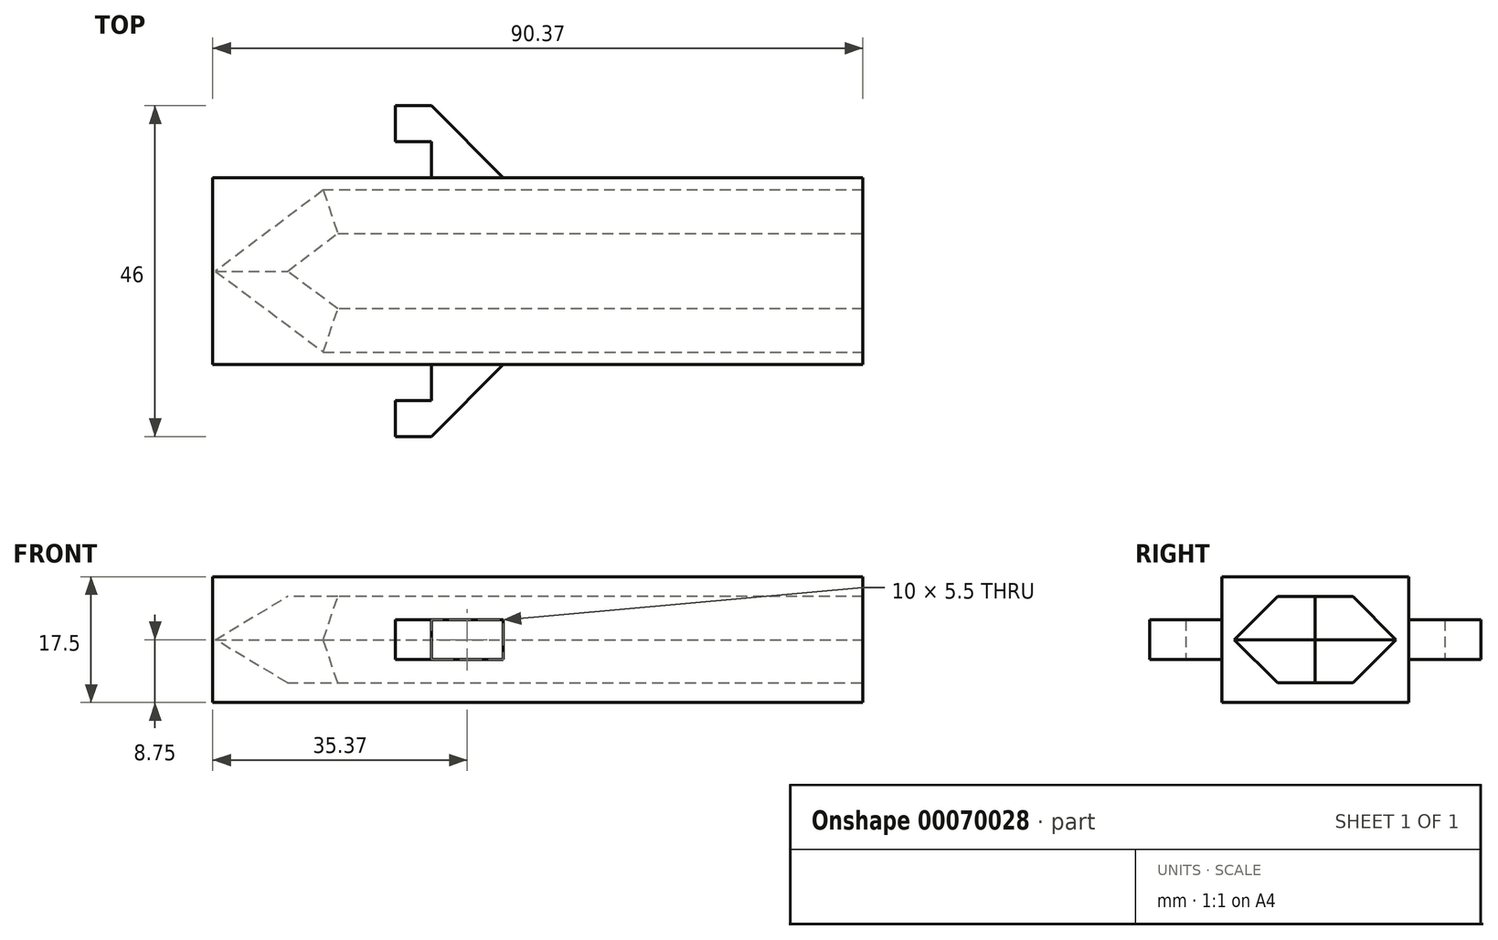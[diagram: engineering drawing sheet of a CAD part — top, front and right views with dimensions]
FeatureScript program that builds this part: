
annotation { "Feature Type Name" : "Feature", "Feature Type Description" : "" }
export const myFeature = defineFeature(function(context is Context, id is Id, definition is map)
    precondition{}
    {
        {
            var Q0;
            Q0=qCreatedBy(makeId("Top.planeOp"),FACE);
            var sketch = newSketch(context, id + "F0", { "sketchPlane" : qUnion([Q0])});
            skLineSegment(sketch, "E0.bottom", {"start": v(0, 0) * mm, "end": v(91, 0) * mm});
            skLineSegment(sketch, "E0.top", {"start": v(0, 21) * mm, "end": v(91, 21) * mm});
            skLineSegment(sketch, "E0.left", {"start": v(0, 0) * mm, "end": v(0, 21) * mm});
            skLineSegment(sketch, "E0.right", {"start": v(91, 0) * mm, "end": v(91, 21) * mm});
            skLineSegment(sketch, "E1", {"start": v(0, 10.5) * mm, "end": v(15, 10.5) * mm});
            skLineSegment(sketch, "E2", {"start": v(0, 10.5) * mm, "end": v(15, 21) * mm});
            skLineSegment(sketch, "E3", {"start": v(0, 10.5) * mm, "end": v(15, 0) * mm});
            skSolve(sketch);
        }
        {
            var Q0;
            Q0 = qSketchRegion(id + "F0", true);
            extrude(context, id + "F1", {"entities" : qUnion([Q0]), "depth" : 10 * mm});
        }
        {
            var Q0;
            Q0=makeQuery(id+"F1.opExtrude","SWEPT_FACE",FACE,{"disambiguationData":[OSD([sQuery(id+"F0.wireOp",EDGE,"E0.left")])]});
            var sketch = newSketch(context, id + "F2", { "sketchPlane" : qUnion([Q0])});
            skSolve(sketch);
        }
        {
            var Q0;
            Q0 = qSketchRegion(id + "F2", true);
            var Q1;
            {var subQ0=sQuery(id+"F0.wireOp",EDGE,"E0.left");Q1=makeQuery(id+"F2.imprint","IMPRINT",FACE,{"disambiguationData":[TD([[makeQuery(id+"F2.imprint","IMPRINT",EDGE,{"derivedFrom":makeQuery(id+"F1.opExtrude","CAP_EDGE",EDGE,{"disambiguationData":[OSD([subQ0])],"isStart":true})}),-1.0]])]});}
            extrude(context, id + "F3", {"entities" : qUnion([Q0, Q1]), "operationType" : NewBodyOperationType.ADD, "depth" : 9 * mm});
        }
        {
            var Q0;
            {var subQ0=sQuery(id+"F0.wireOp",EDGE,"E0.left");Q0=makeQuery(id+"F3.boolean.opBoolean","MERGE",FACE,{"derivedFrom":[makeQuery(id+"F1.opExtrude","CAP_FACE",FACE,{"disambiguationData":[OSD([sQuery(id+"F0.wireOp",EDGE,"E0.bottom"),sQuery(id+"F0.wireOp",EDGE,"E0.top"),subQ0,sQuery(id+"F0.wireOp",EDGE,"E0.right")])],"isStart":false}),makeQuery(id+"F3.opExtrude","SWEPT_FACE",FACE,{"disambiguationData":[OSD([subQ0]),TDD([makeQuery(id+"F2.imprint","IMPRINT",EDGE,{"derivedFrom":makeQuery(id+"F1.opExtrude","CAP_EDGE",EDGE,{"disambiguationData":[OSD([subQ0])],"isStart":false})})])]})]});}
            extrude(context, id + "F4", {"entities" : qUnion([Q0]), "operationType" : NewBodyOperationType.ADD, "depth" : 2 * mm});
        }
        {
            var Q0;
            Q0=makeQuery(id+"F4.opExtrude","CAP_FACE",FACE,{"disambiguationData":[OSD([sQuery(id+"F0.wireOp",EDGE,"E0.bottom"),sQuery(id+"F0.wireOp",EDGE,"E0.top"),sQuery(id+"F0.wireOp",EDGE,"E0.left"),sQuery(id+"F0.wireOp",EDGE,"E0.right")])],"isStart":false});
            extrude(context, id + "F5", {"entities" : qUnion([Q0]), "operationType" : NewBodyOperationType.ADD, "depth" : 3 * mm});
        }
        {
            var Q0;
            {var subQ0=sQuery(id+"F0.wireOp",EDGE,"E0.left");var subQ1=sQuery(id+"F0.wireOp",EDGE,"E0.top");Q0=makeQuery(id+"F5.boolean.opBoolean","MERGE",FACE,{"derivedFrom":[makeQuery(id+"F4.boolean.opBoolean","MERGE",FACE,{"derivedFrom":[makeQuery(id+"F3.boolean.opBoolean","MERGE",FACE,{"derivedFrom":[makeQuery(id+"F1.opExtrude","SWEPT_FACE",FACE,{"disambiguationData":[OSD([subQ1])]}),makeQuery(id+"F3.opExtrude","SWEPT_FACE",FACE,{"disambiguationData":[OSD([subQ1,subQ0])]})]}),makeQuery(id+"F4.opExtrude","SWEPT_FACE",FACE,{"disambiguationData":[OSD([subQ1,subQ0])]})]}),makeQuery(id+"F5.opExtrude","SWEPT_FACE",FACE,{"disambiguationData":[OSD([subQ1,subQ0])]})]});}
            extrude(context, id + "F6", {"entities" : qUnion([Q0]), "operationType" : NewBodyOperationType.ADD, "depth" : 5 * mm});
        }
        {
            var Q0;
            {var subQ0=sQuery(id+"F0.wireOp",EDGE,"E0.left");var subQ1=sQuery(id+"F0.wireOp",EDGE,"E0.top");Q0=makeQuery(id+"F6.boolean.opBoolean","MERGE",FACE,{"derivedFrom":[makeQuery(id+"F5.opExtrude","CAP_FACE",FACE,{"disambiguationData":[OSD([sQuery(id+"F0.wireOp",EDGE,"E0.bottom"),subQ1,subQ0,sQuery(id+"F0.wireOp",EDGE,"E0.right")])],"isStart":false}),makeQuery(id+"F6.opExtrude","SWEPT_FACE",FACE,{"disambiguationData":[OSD([subQ1,subQ0]),TDD([makeQuery(id+"F5.opExtrude","CAP_EDGE",EDGE,{"disambiguationData":[OSD([subQ1,subQ0])],"isStart":false})])]})]});}
            extrude(context, id + "F7", {"entities" : qUnion([Q0]), "operationType" : NewBodyOperationType.ADD, "depth" : 2.5 * mm});
        }
        {
            var Q0;
            {var subQ0=sQuery(id+"F0.wireOp",EDGE,"E0.right");var subQ1=sQuery(id+"F0.wireOp",EDGE,"E0.top");Q0=makeQuery(id+"F7.boolean.opBoolean","MERGE",FACE,{"derivedFrom":[makeQuery(id+"F6.boolean.opBoolean","MERGE",FACE,{"derivedFrom":[makeQuery(id+"F5.boolean.opBoolean","MERGE",FACE,{"derivedFrom":[makeQuery(id+"F4.boolean.opBoolean","MERGE",FACE,{"derivedFrom":[makeQuery(id+"F1.opExtrude","SWEPT_FACE",FACE,{"disambiguationData":[OSD([subQ0])]}),makeQuery(id+"F4.opExtrude","SWEPT_FACE",FACE,{"disambiguationData":[OSD([subQ0])]})]}),makeQuery(id+"F5.opExtrude","SWEPT_FACE",FACE,{"disambiguationData":[OSD([subQ0])]})]}),makeQuery(id+"F6.opExtrude","SWEPT_FACE",FACE,{"disambiguationData":[OSD([subQ1,subQ0])]})]}),makeQuery(id+"F7.opExtrude","SWEPT_FACE",FACE,{"disambiguationData":[OSD([subQ1,subQ0])]})]});}
            var sketch = newSketch(context, id + "F8", { "sketchPlane" : qUnion([Q0])});
            skLineSegment(sketch, "E4.bottom", {"start": v(1.75, 14.75) * mm, "end": v(24.25, 14.75) * mm});
            skLineSegment(sketch, "E4.top", {"start": v(1.75, 2.75) * mm, "end": v(24.25, 2.75) * mm});
            skLineSegment(sketch, "E4.left", {"start": v(1.75, 14.75) * mm, "end": v(1.75, 2.75) * mm});
            skLineSegment(sketch, "E4.right", {"start": v(24.25, 14.75) * mm, "end": v(24.25, 2.75) * mm});
            skSolve(sketch);
        }
        {
            var Q0;
            Q0 = qSketchRegion(id + "F8", true);
            extrude(context, id + "F9", {"entities" : qUnion([Q0]), "operationType" : NewBodyOperationType.REMOVE, "oppositeDirection" : true, "depth" : 75 * mm});
        }
        {
            var Q0;
            Q0=makeQuery(id+"F9.boolean.opBoolean","COPY",FACE,{"derivedFrom":makeQuery(id+"F9.opExtrude","SWEPT_FACE",FACE,{"disambiguationData":[OSD([sQuery(id+"F8.wireOp",EDGE,"E4.top")])]})});
            var sketch = newSketch(context, id + "F10", { "sketchPlane" : qUnion([Q0])});
            skLineSegment(sketch, "E5", {"start": v(16, 13) * mm, "end": v(1, 13) * mm});
            skLineSegment(sketch, "E6", {"start": v(1, 13) * mm, "end": v(16, 24.25) * mm});
            skLineSegment(sketch, "E7", {"start": v(16, 24.25) * mm, "end": v(16, 1.75) * mm});
            skLineSegment(sketch, "E8", {"start": v(16, 1.75) * mm, "end": v(1, 13) * mm});
            skSolve(sketch);
        }
        {
            var Q0;
            Q0 = qSketchRegion(id + "F10", true);
            extrude(context, id + "F11", {"entities" : qUnion([Q0]), "operationType" : NewBodyOperationType.REMOVE, "depth" : 12 * mm});
        }
        {
            var Q0;
            Q0=makeQuery(id+"F11.boolean.opBoolean","COPY",EDGE,{"derivedFrom":makeQuery(id+"F11.opExtrude","CAP_EDGE",EDGE,{"disambiguationData":[OSD([sQuery(id+"F10.wireOp",EDGE,"E8")])],"isStart":false})});
            var Q1;
            Q1=makeQuery(id+"F11.boolean.opBoolean","COPY",EDGE,{"derivedFrom":makeQuery(id+"F11.opExtrude","CAP_EDGE",EDGE,{"disambiguationData":[OSD([sQuery(id+"F10.wireOp",EDGE,"E6")])],"isStart":false})});
            var Q2;
            Q2=makeQuery(id+"F11.boolean.opBoolean","COPY",EDGE,{"derivedFrom":makeQuery(id+"F11.opExtrude","CAP_EDGE",EDGE,{"disambiguationData":[OSD([sQuery(id+"F10.wireOp",EDGE,"E8")])],"isStart":true})});
            var Q3;
            Q3=makeQuery(id+"F11.boolean.opBoolean","COPY",EDGE,{"derivedFrom":makeQuery(id+"F11.opExtrude","CAP_EDGE",EDGE,{"disambiguationData":[OSD([sQuery(id+"F10.wireOp",EDGE,"E6")])],"isStart":true})});
            var Q4;
            Q4=makeQuery(id+"F9.boolean.opBoolean","COPY",EDGE,{"derivedFrom":makeQuery(id+"F9.opExtrude","SWEPT_EDGE",EDGE,{"disambiguationData":[OSD([sQuery(id+"F8.wireOp",EDGE,"E4.top"),sQuery(id+"F8.wireOp",EDGE,"E4.left")])]})});
            var Q5;
            Q5=makeQuery(id+"F9.boolean.opBoolean","COPY",EDGE,{"derivedFrom":makeQuery(id+"F9.opExtrude","SWEPT_EDGE",EDGE,{"disambiguationData":[OSD([sQuery(id+"F8.wireOp",EDGE,"E4.bottom"),sQuery(id+"F8.wireOp",EDGE,"E4.left")])]})});
            var Q6;
            Q6=makeQuery(id+"F9.boolean.opBoolean","COPY",EDGE,{"derivedFrom":makeQuery(id+"F9.opExtrude","SWEPT_EDGE",EDGE,{"disambiguationData":[OSD([sQuery(id+"F8.wireOp",EDGE,"E4.bottom"),sQuery(id+"F8.wireOp",EDGE,"E4.right")])]})});
            var Q7;
            Q7=makeQuery(id+"F9.boolean.opBoolean","COPY",EDGE,{"derivedFrom":makeQuery(id+"F9.opExtrude","SWEPT_EDGE",EDGE,{"disambiguationData":[OSD([sQuery(id+"F8.wireOp",EDGE,"E4.top"),sQuery(id+"F8.wireOp",EDGE,"E4.right")])]})});
            chamfer(context, id + "F12", {"entities" : qUnion([Q0, Q1, Q2, Q3, Q4, Q5, Q6, Q7]), "width" : 6 * mm, "tangentPropagation" : true});
        }
        {
            var Q0;
            {var subQ0=sQuery(id+"F0.wireOp",EDGE,"E0.left");var subQ1=sQuery(id+"F0.wireOp",EDGE,"E0.top");Q0=makeQuery(id+"F7.boolean.opBoolean","MERGE",FACE,{"derivedFrom":[makeQuery(id+"F6.opExtrude","CAP_FACE",FACE,{"disambiguationData":[OSD([subQ1,subQ0])],"isStart":false}),makeQuery(id+"F7.opExtrude","SWEPT_FACE",FACE,{"disambiguationData":[OSD([subQ1,subQ0]),TDD([makeQuery(id+"F6.opExtrude","CAP_EDGE",EDGE,{"disambiguationData":[OSD([subQ1,subQ0]),TDD([makeQuery(id+"F5.opExtrude","CAP_EDGE",EDGE,{"disambiguationData":[OSD([subQ1,subQ0])],"isStart":false})])],"isStart":false})])]})]});}
            var sketch = newSketch(context, id + "F13", { "sketchPlane" : qUnion([Q0])});
            skPoint(sketch, "E9.firstSnap0", {"position": v(-41, 17.5) * mm});
            skLineSegment(sketch, "E9.bottom", {"start": v(-41, 11.5) * mm, "end": v(-26, 11.5) * mm});
            skLineSegment(sketch, "E9.top", {"start": v(-41, 6) * mm, "end": v(-26, 6) * mm});
            skLineSegment(sketch, "E9.left", {"start": v(-41, 11.5) * mm, "end": v(-41, 6) * mm});
            skLineSegment(sketch, "E9.right", {"start": v(-26, 11.5) * mm, "end": v(-26, 6) * mm});
            skLineSegment(sketch, "E10", {"start": v(-91, 17.5) * mm, "end": v(-91, 0) * mm});
            skSolve(sketch);
        }
        {
            var Q0;
            Q0 = qSketchRegion(id + "F13", true);
            extrude(context, id + "F14", {"entities" : qUnion([Q0]), "operationType" : NewBodyOperationType.ADD, "depth" : 10 * mm});
        }
        {
            var Q0;
            Q0=makeQuery(id+"F14.opExtrude","CAP_EDGE",EDGE,{"disambiguationData":[OSD([sQuery(id+"F13.wireOp",EDGE,"E9.left")])],"isStart":false});
            chamfer(context, id + "F15", {"entities" : qUnion([Q0]), "width" : 10 * mm, "tangentPropagation" : true});
        }
        {
            var Q0;
            Q0=makeQuery(id+"F14.opExtrude","SWEPT_FACE",FACE,{"disambiguationData":[OSD([sQuery(id+"F13.wireOp",EDGE,"E9.right")])]});
            var sketch = newSketch(context, id + "F16", { "sketchPlane" : qUnion([Q0])});
            skLineSegment(sketch, "E11.bottom", {"start": v(-31, 11.5) * mm, "end": v(-26, 11.5) * mm});
            skLineSegment(sketch, "E11.top", {"start": v(-31, 6) * mm, "end": v(-26, 6) * mm});
            skLineSegment(sketch, "E11.left", {"start": v(-31, 11.5) * mm, "end": v(-31, 6) * mm});
            skLineSegment(sketch, "E11.right", {"start": v(-26, 11.5) * mm, "end": v(-26, 6) * mm});
            skSolve(sketch);
        }
        {
            var Q0;
            Q0 = qSketchRegion(id + "F16", true);
            extrude(context, id + "F17", {"entities" : qUnion([Q0]), "operationType" : NewBodyOperationType.REMOVE, "oppositeDirection" : true, "depth" : 5 * mm});
        }
        {
            var Q0;
            {var subQ0=sQuery(id+"F0.wireOp",EDGE,"E0.left");var subQ1=sQuery(id+"F0.wireOp",EDGE,"E0.bottom");Q0=makeQuery(id+"F7.boolean.opBoolean","MERGE",FACE,{"derivedFrom":[makeQuery(id+"F5.boolean.opBoolean","MERGE",FACE,{"derivedFrom":[makeQuery(id+"F4.boolean.opBoolean","MERGE",FACE,{"derivedFrom":[makeQuery(id+"F3.boolean.opBoolean","MERGE",FACE,{"derivedFrom":[makeQuery(id+"F1.opExtrude","SWEPT_FACE",FACE,{"disambiguationData":[OSD([subQ1])]}),makeQuery(id+"F3.opExtrude","SWEPT_FACE",FACE,{"disambiguationData":[OSD([subQ1,subQ0])]})]}),makeQuery(id+"F4.opExtrude","SWEPT_FACE",FACE,{"disambiguationData":[OSD([subQ1,subQ0])]})]}),makeQuery(id+"F5.opExtrude","SWEPT_FACE",FACE,{"disambiguationData":[OSD([subQ1,subQ0])]})]}),makeQuery(id+"F7.opExtrude","SWEPT_FACE",FACE,{"disambiguationData":[OSD([subQ1,subQ0])]})]});}
            var sketch = newSketch(context, id + "F18", { "sketchPlane" : qUnion([Q0])});
            skPoint(sketch, "E12.firstSnap0", {"position": v(41, 17.5) * mm});
            skLineSegment(sketch, "E12.bottom", {"start": v(41, 11.5) * mm, "end": v(26, 11.5) * mm});
            skLineSegment(sketch, "E12.top", {"start": v(41, 6) * mm, "end": v(26, 6) * mm});
            skLineSegment(sketch, "E12.left", {"start": v(41, 11.5) * mm, "end": v(41, 6) * mm});
            skLineSegment(sketch, "E12.right", {"start": v(26, 11.5) * mm, "end": v(26, 6) * mm});
            skSolve(sketch);
        }
        {
            var Q0;
            Q0 = qSketchRegion(id + "F18", true);
            extrude(context, id + "F19", {"entities" : qUnion([Q0]), "operationType" : NewBodyOperationType.ADD, "depth" : 10 * mm});
        }
        {
            var Q0;
            Q0=makeQuery(id+"F19.opExtrude","CAP_EDGE",EDGE,{"disambiguationData":[OSD([sQuery(id+"F18.wireOp",EDGE,"E12.left")])],"isStart":false});
            chamfer(context, id + "F20", {"entities" : qUnion([Q0]), "width" : 10 * mm, "tangentPropagation" : true});
        }
        {
            var Q0;
            Q0=makeQuery(id+"F19.opExtrude","SWEPT_FACE",FACE,{"disambiguationData":[OSD([sQuery(id+"F18.wireOp",EDGE,"E12.right")])]});
            var sketch = newSketch(context, id + "F21", { "sketchPlane" : qUnion([Q0])});
            skLineSegment(sketch, "E13.bottom", {"start": v(0, 11.5) * mm, "end": v(5, 11.5) * mm});
            skLineSegment(sketch, "E13.top", {"start": v(0, 6) * mm, "end": v(5, 6) * mm});
            skLineSegment(sketch, "E13.left", {"start": v(0, 11.5) * mm, "end": v(0, 6) * mm});
            skLineSegment(sketch, "E13.right", {"start": v(5, 11.5) * mm, "end": v(5, 6) * mm});
            skSolve(sketch);
        }
        {
            var Q0;
            Q0 = qSketchRegion(id + "F21", true);
            extrude(context, id + "F22", {"entities" : qUnion([Q0]), "operationType" : NewBodyOperationType.REMOVE, "oppositeDirection" : true, "depth" : 5 * mm});
        }
        {
            var Q0;
            {var subQ0=sQuery(id+"F0.wireOp",EDGE,"E0.left");var subQ1=sQuery(id+"F0.wireOp",EDGE,"E0.top");Q0=makeQuery(id+"F7.boolean.opBoolean","MERGE",FACE,{"derivedFrom":[makeQuery(id+"F6.boolean.opBoolean","MERGE",FACE,{"derivedFrom":[makeQuery(id+"F5.boolean.opBoolean","MERGE",FACE,{"derivedFrom":[makeQuery(id+"F4.boolean.opBoolean","MERGE",FACE,{"derivedFrom":[makeQuery(id+"F3.opExtrude","CAP_FACE",FACE,{"disambiguationData":[OSD([sQuery(id+"F0.wireOp",EDGE,"E0.bottom"),subQ1,subQ0])],"isStart":false}),makeQuery(id+"F4.opExtrude","SWEPT_FACE",FACE,{"disambiguationData":[OSD([subQ0])]})]}),makeQuery(id+"F5.opExtrude","SWEPT_FACE",FACE,{"disambiguationData":[OSD([subQ0])]})]}),makeQuery(id+"F6.opExtrude","SWEPT_FACE",FACE,{"disambiguationData":[OSD([subQ1,subQ0]),TDD([makeQuery(id+"F5.boolean.opBoolean","MERGE",EDGE,{"derivedFrom":[makeQuery(id+"F4.boolean.opBoolean","MERGE",EDGE,{"derivedFrom":[makeQuery(id+"F3.opExtrude","CAP_EDGE",EDGE,{"disambiguationData":[OSD([subQ1,subQ0])],"isStart":false}),makeQuery(id+"F4.opExtrude","SWEPT_EDGE",EDGE,{"disambiguationData":[OSD([subQ1,subQ0])]})]}),makeQuery(id+"F5.opExtrude","SWEPT_EDGE",EDGE,{"disambiguationData":[OSD([subQ1,subQ0])]})]})])]})]}),makeQuery(id+"F7.opExtrude","SWEPT_FACE",FACE,{"disambiguationData":[OSD([subQ1,subQ0]),TDD([makeQuery(id+"F6.boolean.opBoolean","MERGE",EDGE,{"derivedFrom":[makeQuery(id+"F5.opExtrude","CAP_EDGE",EDGE,{"disambiguationData":[OSD([subQ0])],"isStart":false}),makeQuery(id+"F6.opExtrude","SWEPT_EDGE",EDGE,{"disambiguationData":[OSD([subQ1,subQ0]),TDD([makeQuery(id+"F5.opExtrude","CAP_VERTEX",VERTEX,{"disambiguationData":[OSD([subQ1,subQ0])],"isStart":false})])]})]})])]})]});}
            extrude(context, id + "F23", {"entities" : qUnion([Q0]), "operationType" : NewBodyOperationType.ADD, "depth" : 5 * mm});
        }
        {
            var Q0;
            {var subQ0=sQuery(id+"F0.wireOp",EDGE,"E0.left");var subQ1=sQuery(id+"F0.wireOp",EDGE,"E0.top");Q0=makeQuery(id+"F23.opExtrude","CAP_EDGE",EDGE,{"disambiguationData":[OSD([subQ1,subQ0]),TDD([makeQuery(id+"F7.boolean.opBoolean","MERGE",EDGE,{"derivedFrom":[makeQuery(id+"F6.opExtrude","CAP_EDGE",EDGE,{"disambiguationData":[OSD([subQ1,subQ0]),TDD([makeQuery(id+"F5.boolean.opBoolean","MERGE",EDGE,{"derivedFrom":[makeQuery(id+"F4.boolean.opBoolean","MERGE",EDGE,{"derivedFrom":[makeQuery(id+"F3.opExtrude","CAP_EDGE",EDGE,{"disambiguationData":[OSD([subQ1,subQ0])],"isStart":false}),makeQuery(id+"F4.opExtrude","SWEPT_EDGE",EDGE,{"disambiguationData":[OSD([subQ1,subQ0])]})]}),makeQuery(id+"F5.opExtrude","SWEPT_EDGE",EDGE,{"disambiguationData":[OSD([subQ1,subQ0])]})]})])],"isStart":false}),makeQuery(id+"F7.opExtrude","SWEPT_EDGE",EDGE,{"disambiguationData":[OSD([subQ1,subQ0])]})]})])],"isStart":false});}
            var Q1;
            {var subQ0=sQuery(id+"F0.wireOp",EDGE,"E0.left");var subQ1=sQuery(id+"F0.wireOp",EDGE,"E0.top");Q1=makeQuery(id+"F23.opExtrude","CAP_EDGE",EDGE,{"disambiguationData":[OSD([subQ1,subQ0]),TDD([makeQuery(id+"F7.opExtrude","CAP_EDGE",EDGE,{"disambiguationData":[OSD([subQ1,subQ0]),TDD([makeQuery(id+"F6.boolean.opBoolean","MERGE",EDGE,{"derivedFrom":[makeQuery(id+"F5.opExtrude","CAP_EDGE",EDGE,{"disambiguationData":[OSD([subQ0])],"isStart":false}),makeQuery(id+"F6.opExtrude","SWEPT_EDGE",EDGE,{"disambiguationData":[OSD([subQ1,subQ0]),TDD([makeQuery(id+"F5.opExtrude","CAP_VERTEX",VERTEX,{"disambiguationData":[OSD([subQ1,subQ0])],"isStart":false})])]})]})])],"isStart":false})])],"isStart":false});}
            var Q2;
            Q2=makeQuery(id+"F23.opExtrude","CAP_EDGE",EDGE,{"disambiguationData":[OSD([sQuery(id+"F0.wireOp",EDGE,"E0.bottom"),sQuery(id+"F0.wireOp",EDGE,"E0.left")])],"isStart":false});
            var Q3;
            {var subQ0=sQuery(id+"F0.wireOp",EDGE,"E0.left");var subQ1=makeQuery(id+"F1.opExtrude","CAP_EDGE",EDGE,{"disambiguationData":[OSD([subQ0])],"isStart":true});var subQ2=sQuery(id+"F0.wireOp",EDGE,"E0.top");Q3=makeQuery(id+"F23.opExtrude","CAP_EDGE",EDGE,{"disambiguationData":[OSD([subQ2,subQ0]),TDD([makeQuery(id+"F6.boolean.opBoolean","MERGE",EDGE,{"derivedFrom":[makeQuery(id+"F3.opExtrude","CAP_EDGE",EDGE,{"disambiguationData":[OSD([subQ0]),TDD([makeQuery(id+"F2.imprint","IMPRINT",EDGE,{"derivedFrom":subQ1})])],"isStart":false}),makeQuery(id+"F6.opExtrude","SWEPT_EDGE",EDGE,{"disambiguationData":[OSD([subQ2,subQ0]),TDD([makeQuery(id+"F3.opExtrude","CAP_VERTEX",VERTEX,{"disambiguationData":[OSD([subQ2,subQ0]),TDD([makeQuery(id+"F2.imprint","INTERSECT",VERTEX,{"derivedFrom":[makeQuery(id+"F1.opExtrude","SWEPT_EDGE",EDGE,{"disambiguationData":[OSD([subQ2,subQ0])]}),subQ1]})])],"isStart":false})])]})]})])],"isStart":false});}
            chamfer(context, id + "F24", {"entities" : qUnion([Q0, Q1, Q2, Q3]), "width" : 5 * mm, "tangentPropagation" : true});
        }
        {
            var Q0;
            Q0=makeQuery(id+"F23.opExtrude","CAP_FACE",FACE,{"disambiguationData":[OSD([sQuery(id+"F0.wireOp",EDGE,"E0.bottom"),sQuery(id+"F0.wireOp",EDGE,"E0.top"),sQuery(id+"F0.wireOp",EDGE,"E0.left")])],"isStart":false});
            extrude(context, id + "F25", {"entities" : qUnion([Q0]), "operationType" : NewBodyOperationType.ADD, "depth" : 5 * mm});
        }
        {
            var Q0;
            {var subQ0=sQuery(id+"F0.wireOp",EDGE,"E0.left");var subQ1=sQuery(id+"F0.wireOp",EDGE,"E0.top");var subQ2=sQuery(id+"F0.wireOp",EDGE,"E0.bottom");Q0=makeQuery(id+"F25.opExtrude","CAP_EDGE",EDGE,{"disambiguationData":[OSD([subQ2,subQ1,subQ0]),TDD([makeQuery(id+"F24.opChamfer","BLEND_EDGE",EDGE,{"blendedFrom":[makeQuery(id+"F23.opExtrude","CAP_EDGE",EDGE,{"disambiguationData":[OSD([subQ1,subQ0]),TDD([makeQuery(id+"F7.opExtrude","CAP_EDGE",EDGE,{"disambiguationData":[OSD([subQ1,subQ0]),TDD([makeQuery(id+"F6.boolean.opBoolean","MERGE",EDGE,{"derivedFrom":[makeQuery(id+"F5.opExtrude","CAP_EDGE",EDGE,{"disambiguationData":[OSD([subQ0])],"isStart":false}),makeQuery(id+"F6.opExtrude","SWEPT_EDGE",EDGE,{"disambiguationData":[OSD([subQ1,subQ0]),TDD([makeQuery(id+"F5.opExtrude","CAP_VERTEX",VERTEX,{"disambiguationData":[OSD([subQ1,subQ0])],"isStart":false})])]})]})])],"isStart":false})])],"isStart":false}),makeQuery(id+"F23.opExtrude","CAP_FACE",FACE,{"disambiguationData":[OSD([subQ2,subQ1,subQ0])],"isStart":false})],"blendedInto":[makeQuery(id+"F23.opExtrude","CAP_FACE",FACE,{"disambiguationData":[OSD([subQ2,subQ1,subQ0])],"isStart":false})]})])],"isStart":false});}
            var Q1;
            {var subQ0=sQuery(id+"F0.wireOp",EDGE,"E0.left");var subQ1=sQuery(id+"F0.wireOp",EDGE,"E0.top");var subQ2=sQuery(id+"F0.wireOp",EDGE,"E0.bottom");Q1=makeQuery(id+"F25.opExtrude","CAP_EDGE",EDGE,{"disambiguationData":[OSD([subQ2,subQ1,subQ0]),TDD([makeQuery(id+"F24.opChamfer","BLEND_EDGE",EDGE,{"blendedFrom":[makeQuery(id+"F23.opExtrude","CAP_EDGE",EDGE,{"disambiguationData":[OSD([subQ1,subQ0]),TDD([makeQuery(id+"F7.boolean.opBoolean","MERGE",EDGE,{"derivedFrom":[makeQuery(id+"F6.opExtrude","CAP_EDGE",EDGE,{"disambiguationData":[OSD([subQ1,subQ0]),TDD([makeQuery(id+"F5.boolean.opBoolean","MERGE",EDGE,{"derivedFrom":[makeQuery(id+"F4.boolean.opBoolean","MERGE",EDGE,{"derivedFrom":[makeQuery(id+"F3.opExtrude","CAP_EDGE",EDGE,{"disambiguationData":[OSD([subQ1,subQ0])],"isStart":false}),makeQuery(id+"F4.opExtrude","SWEPT_EDGE",EDGE,{"disambiguationData":[OSD([subQ1,subQ0])]})]}),makeQuery(id+"F5.opExtrude","SWEPT_EDGE",EDGE,{"disambiguationData":[OSD([subQ1,subQ0])]})]})])],"isStart":false}),makeQuery(id+"F7.opExtrude","SWEPT_EDGE",EDGE,{"disambiguationData":[OSD([subQ1,subQ0])]})]})])],"isStart":false}),makeQuery(id+"F23.opExtrude","CAP_FACE",FACE,{"disambiguationData":[OSD([subQ2,subQ1,subQ0])],"isStart":false})],"blendedInto":[makeQuery(id+"F23.opExtrude","CAP_FACE",FACE,{"disambiguationData":[OSD([subQ2,subQ1,subQ0])],"isStart":false})]})])],"isStart":false});}
            var Q2;
            {var subQ0=sQuery(id+"F0.wireOp",EDGE,"E0.left");var subQ1=sQuery(id+"F0.wireOp",EDGE,"E0.top");var subQ2=sQuery(id+"F0.wireOp",EDGE,"E0.bottom");var subQ3=makeQuery(id+"F1.opExtrude","CAP_EDGE",EDGE,{"disambiguationData":[OSD([subQ0])],"isStart":true});Q2=makeQuery(id+"F25.opExtrude","CAP_EDGE",EDGE,{"disambiguationData":[OSD([subQ2,subQ1,subQ0]),TDD([makeQuery(id+"F24.opChamfer","BLEND_EDGE",EDGE,{"blendedFrom":[makeQuery(id+"F23.opExtrude","CAP_EDGE",EDGE,{"disambiguationData":[OSD([subQ1,subQ0]),TDD([makeQuery(id+"F6.boolean.opBoolean","MERGE",EDGE,{"derivedFrom":[makeQuery(id+"F3.opExtrude","CAP_EDGE",EDGE,{"disambiguationData":[OSD([subQ0]),TDD([makeQuery(id+"F2.imprint","IMPRINT",EDGE,{"derivedFrom":subQ3})])],"isStart":false}),makeQuery(id+"F6.opExtrude","SWEPT_EDGE",EDGE,{"disambiguationData":[OSD([subQ1,subQ0]),TDD([makeQuery(id+"F3.opExtrude","CAP_VERTEX",VERTEX,{"disambiguationData":[OSD([subQ1,subQ0]),TDD([makeQuery(id+"F2.imprint","INTERSECT",VERTEX,{"derivedFrom":[makeQuery(id+"F1.opExtrude","SWEPT_EDGE",EDGE,{"disambiguationData":[OSD([subQ1,subQ0])]}),subQ3]})])],"isStart":false})])]})]})])],"isStart":false}),makeQuery(id+"F23.opExtrude","CAP_FACE",FACE,{"disambiguationData":[OSD([subQ2,subQ1,subQ0])],"isStart":false})],"blendedInto":[makeQuery(id+"F23.opExtrude","CAP_FACE",FACE,{"disambiguationData":[OSD([subQ2,subQ1,subQ0])],"isStart":false})]})])],"isStart":false});}
            var Q3;
            {var subQ0=sQuery(id+"F0.wireOp",EDGE,"E0.left");var subQ1=sQuery(id+"F0.wireOp",EDGE,"E0.top");var subQ2=sQuery(id+"F0.wireOp",EDGE,"E0.bottom");Q3=makeQuery(id+"F25.opExtrude","CAP_EDGE",EDGE,{"disambiguationData":[OSD([subQ2,subQ1,subQ0]),TDD([makeQuery(id+"F24.opChamfer","BLEND_EDGE",EDGE,{"blendedFrom":[makeQuery(id+"F23.opExtrude","CAP_EDGE",EDGE,{"disambiguationData":[OSD([subQ2,subQ0])],"isStart":false}),makeQuery(id+"F23.opExtrude","CAP_FACE",FACE,{"disambiguationData":[OSD([subQ2,subQ1,subQ0])],"isStart":false})],"blendedInto":[makeQuery(id+"F23.opExtrude","CAP_FACE",FACE,{"disambiguationData":[OSD([subQ2,subQ1,subQ0])],"isStart":false})]})])],"isStart":false});}
            chamfer(context, id + "F26", {"entities" : qUnion([Q0, Q1, Q2, Q3]), "width" : 3.75 * mm, "tangentPropagation" : true});
        }
        {
            var Q0;
            Q0=makeQuery(id+"F11.boolean.opBoolean","MERGE",FACE,{"derivedFrom":[makeQuery(id+"F9.boolean.opBoolean","COPY",FACE,{"derivedFrom":makeQuery(id+"F9.opExtrude","SWEPT_FACE",FACE,{"disambiguationData":[OSD([sQuery(id+"F8.wireOp",EDGE,"E4.top")])]})}),makeQuery(id+"F11.opExtrude","CAP_FACE",FACE,{"disambiguationData":[OSD([sQuery(id+"F10.wireOp",EDGE,"E6"),sQuery(id+"F10.wireOp",EDGE,"E7"),sQuery(id+"F10.wireOp",EDGE,"E8")])],"isStart":true})]});
            var sketch = newSketch(context, id + "F27", { "sketchPlane" : qUnion([Q0])});
            skSolve(sketch);
        }
        {
            var Q0;
            {var subQ0=sQuery(id+"F0.wireOp",EDGE,"E0.left");var subQ1=sQuery(id+"F0.wireOp",EDGE,"E0.top");Q0=makeQuery(id+"F23.boolean.opBoolean","MERGE",FACE,{"derivedFrom":[makeQuery(id+"F7.opExtrude","CAP_FACE",FACE,{"disambiguationData":[OSD([sQuery(id+"F0.wireOp",EDGE,"E0.bottom"),subQ1,subQ0,sQuery(id+"F0.wireOp",EDGE,"E0.right")])],"isStart":false}),makeQuery(id+"F23.opExtrude","SWEPT_FACE",FACE,{"disambiguationData":[OSD([subQ1,subQ0]),TDD([makeQuery(id+"F7.opExtrude","CAP_EDGE",EDGE,{"disambiguationData":[OSD([subQ1,subQ0]),TDD([makeQuery(id+"F6.boolean.opBoolean","MERGE",EDGE,{"derivedFrom":[makeQuery(id+"F5.opExtrude","CAP_EDGE",EDGE,{"disambiguationData":[OSD([subQ0])],"isStart":false}),makeQuery(id+"F6.opExtrude","SWEPT_EDGE",EDGE,{"disambiguationData":[OSD([subQ1,subQ0]),TDD([makeQuery(id+"F5.opExtrude","CAP_VERTEX",VERTEX,{"disambiguationData":[OSD([subQ1,subQ0])],"isStart":false})])]})]})])],"isStart":false})])]})]});}
            var sketch = newSketch(context, id + "F28", { "sketchPlane" : qUnion([Q0])});
            skLineSegment(sketch, "E14", {"start": v(11.63, 13) * mm, "end": v(0.63, 13) * mm});
            skLineSegment(sketch, "E15.bottom", {"start": v(0.63, 0) * mm, "end": v(-36.37, 0) * mm});
            skLineSegment(sketch, "E15.top", {"start": v(0.63, 34.46) * mm, "end": v(-36.37, 34.46) * mm});
            skLineSegment(sketch, "E15.left", {"start": v(0.63, 0) * mm, "end": v(0.63, 34.46) * mm});
            skLineSegment(sketch, "E15.right", {"start": v(-36.37, 0) * mm, "end": v(-36.37, 34.46) * mm});
            skSolve(sketch);
        }
        {
            var Q0;
            Q0 = qSketchRegion(id + "F28", true);
            extrude(context, id + "F29", {"entities" : qUnion([Q0]), "operationType" : NewBodyOperationType.REMOVE, "oppositeDirection" : true, "depth" : 25 * mm});
        }
    });
